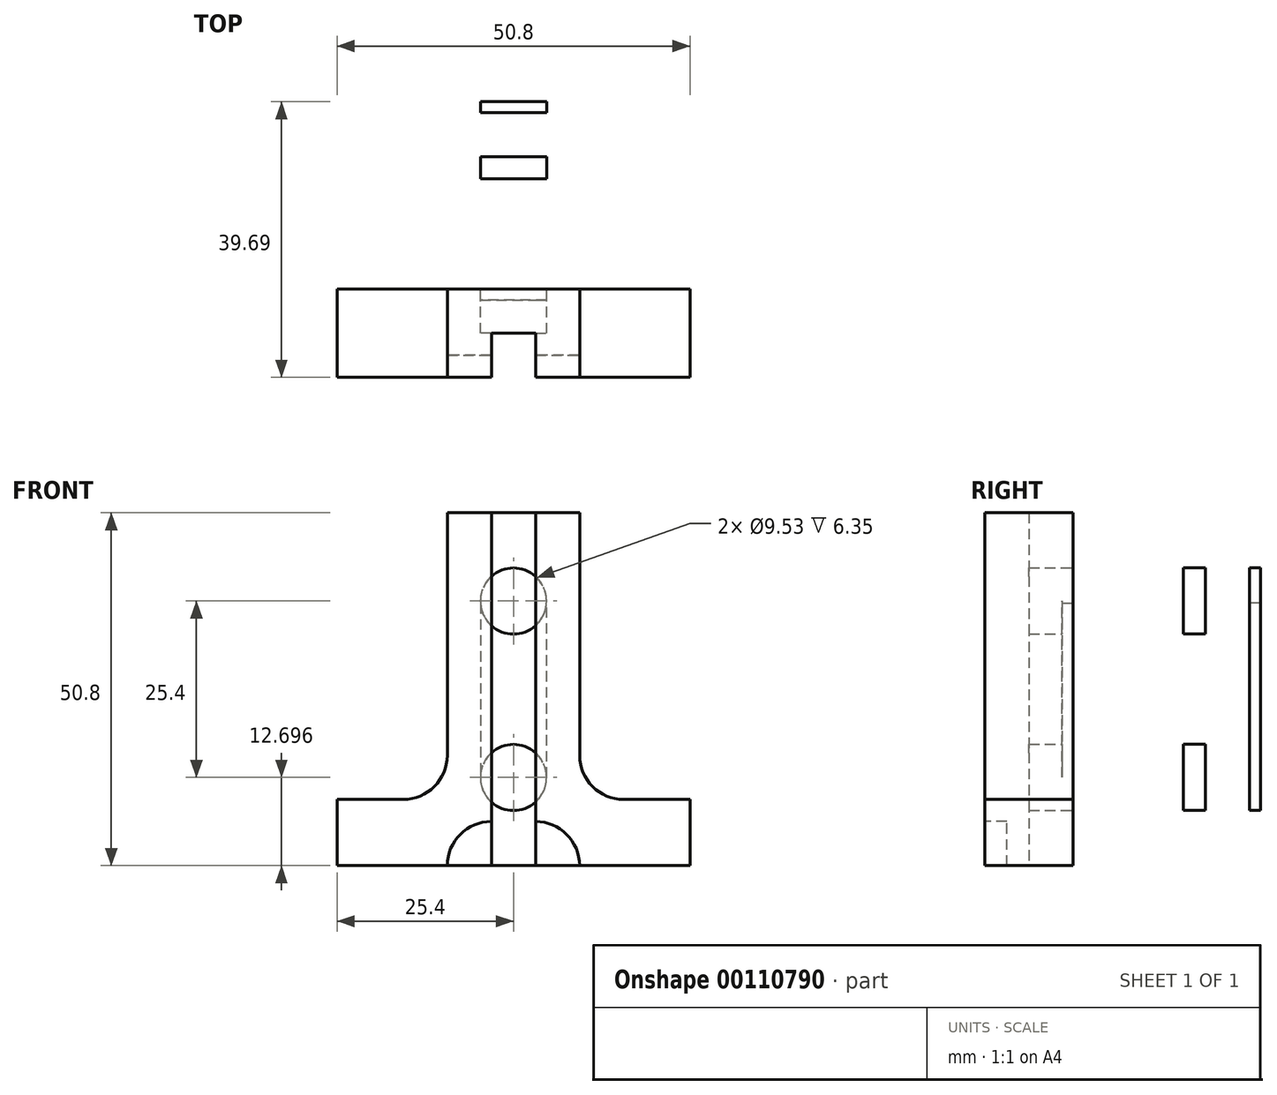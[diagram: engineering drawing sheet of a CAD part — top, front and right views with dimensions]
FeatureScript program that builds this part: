
annotation { "Feature Type Name" : "Feature", "Feature Type Description" : "" }
export const myFeature = defineFeature(function(context is Context, id is Id, definition is map)
    precondition{}
    {
        {
            var Q0;
            Q0=qCreatedBy(makeId("Front.planeOp"),FACE);
            var sketch = newSketch(context, id + "F0", { "sketchPlane" : qUnion([Q0])});
            skLineSegment(sketch, "E0.bottom", {"start": v(-9.52, 21.48) * mm, "end": v(9.53, 21.48) * mm});
            skLineSegment(sketch, "E0.top", {"start": v(-25.4, -29.32) * mm, "end": v(25.4, -29.32) * mm});
            skLineSegment(sketch, "E0.left", {"start": v(-25.4, -19.8) * mm, "end": v(-25.4, -29.32) * mm});
            skLineSegment(sketch, "E0.right", {"start": v(25.4, -19.8) * mm, "end": v(25.4, -29.32) * mm});
            skPoint(sketch, "E0.middle", {"position": v(0, -3.92) * mm});
            skLineSegment(sketch, "E1.bottom", {"start": v(-83.32, -5.3) * mm, "end": v(-91.63, -5.3) * mm});
            skLineSegment(sketch, "E1.top", {"start": v(-83.32, -3.46) * mm, "end": v(-91.63, -3.46) * mm});
            skLineSegment(sketch, "E1.left", {"start": v(-83.32, -5.3) * mm, "end": v(-83.32, -3.46) * mm});
            skLineSegment(sketch, "E1.right", {"start": v(-91.63, -5.3) * mm, "end": v(-91.63, -3.46) * mm});
            skPoint(sketch, "E1.middle", {"position": v(-87.47, -4.39) * mm});
            skLineSegment(sketch, "E2", {"start": v(-25.4, -19.8) * mm, "end": v(-15.88, -19.8) * mm});
            skLineSegment(sketch, "E3", {"start": v(-9.52, 21.48) * mm, "end": v(-9.53, -13.45) * mm});
            skPoint(sketch, "E3.endSnap0", {"position": v(0, -19.8) * mm});
            skLineSegment(sketch, "E4", {"start": v(9.53, 21.48) * mm, "end": v(9.53, -13.45) * mm});
            skPoint(sketch, "E5.orphan", {"position": v(-25.4, 21.48) * mm});
            skPoint(sketch, "E6.orphan", {"position": v(25.4, 21.48) * mm});
            skPoint(sketch, "E7.newPointA", {"position": v(-9.53, -19.8) * mm});
            skPoint(sketch, "E7.newPointB", {"position": v(25.4, -19.8) * mm});
            skArc(sketch, "E7.filletArc", {"start": v(-15.88, -19.8) * mm, "mid": v(-11.38, -17.94) * mm, "end": v(-9.53, -13.45) * mm});
            skLineSegment(sketch, "E8", {"start": v(15.87, -19.8) * mm, "end": v(25.4, -19.8) * mm});
            skPoint(sketch, "E9.visualSharp", {"position": v(9.52, -19.8) * mm});
            skArc(sketch, "E9.filletArc", {"start": v(9.52, -13.45) * mm, "mid": v(11.38, -17.94) * mm, "end": v(15.87, -19.8) * mm});
            skSolve(sketch);
        }
        {
            var Q0;
            Q0 = qSketchRegion(id + "F0", true);
            extrude(context, id + "F1", {"entities" : qUnion([Q0]), "depth" : 12.7 * mm});
        }
        {
            var Q0;
            Q0=makeQuery(id+"F1.opExtrude","CAP_FACE",FACE,{"disambiguationData":[OSD([sQuery(id+"F0.wireOp",EDGE,"E0.bottom"),sQuery(id+"F0.wireOp",EDGE,"E0.top"),sQuery(id+"F0.wireOp",EDGE,"E0.left"),sQuery(id+"F0.wireOp",EDGE,"E0.right"),sQuery(id+"F0.wireOp",EDGE,"E2"),sQuery(id+"F0.wireOp",EDGE,"E3"),sQuery(id+"F0.wireOp",EDGE,"E4"),sQuery(id+"F0.wireOp",EDGE,"E7.filletArc"),sQuery(id+"F0.wireOp",EDGE,"E8"),sQuery(id+"F0.wireOp",EDGE,"E9.filletArc")])],"isStart":false});
            var sketch = newSketch(context, id + "F2", { "sketchPlane" : qUnion([Q0])});
            skLineSegment(sketch, "E10", {"start": v(-3.18, 21.48) * mm, "end": v(-3.18, -29.32) * mm});
            skLineSegment(sketch, "E11", {"start": v(3.18, 21.48) * mm, "end": v(3.18, -29.32) * mm});
            skSolve(sketch);
        }
        {
            var Q0;
            Q0 = qSketchRegion(id + "F2", true);
            var Q1;
            {var subQ0=sQuery(id+"F2.wireOp",EDGE,"E10");Q1=makeQuery(id+"F2.imprint","IMPRINT",FACE,{"disambiguationData":[TD([[makeQuery(id+"F2.imprint","IMPRINT",EDGE,{"derivedFrom":subQ0}),1.0]])]});}
            extrude(context, id + "F3", {"entities" : qUnion([Q0, Q1]), "operationType" : NewBodyOperationType.REMOVE, "oppositeDirection" : true, "depth" : 6.35 * mm});
        }
        {
            var Q0;
            {var subQ0=sQuery(id+"F0.wireOp",EDGE,"E0.right");var subQ1=sQuery(id+"F0.wireOp",EDGE,"E0.top");var subQ2=sQuery(id+"F0.wireOp",EDGE,"E4");var subQ3=sQuery(id+"F0.wireOp",EDGE,"E0.bottom");var subQ4=sQuery(id+"F0.wireOp",EDGE,"E8");var subQ5=sQuery(id+"F0.wireOp",EDGE,"E9.filletArc");Q0=makeQuery(id+"F3.boolean.opBoolean","SPLIT",FACE,{"disambiguationData":[TD([makeQuery(id+"F1.opExtrude","SWEPT_FACE",FACE,{"disambiguationData":[OSD([subQ0])]})])],"derivedFrom":makeQuery(id+"F1.opExtrude","CAP_FACE",FACE,{"disambiguationData":[OSD([subQ3,subQ1,sQuery(id+"F0.wireOp",EDGE,"E0.left"),subQ0,sQuery(id+"F0.wireOp",EDGE,"E2"),sQuery(id+"F0.wireOp",EDGE,"E3"),subQ2,sQuery(id+"F0.wireOp",EDGE,"E7.filletArc"),subQ4,subQ5])],"isStart":false})});}
            var sketch = newSketch(context, id + "F4", { "sketchPlane" : qUnion([Q0])});
            skCircle(sketch, "E12", {"center": v(-3.18, -29.32) * mm, "radius": 6.35 * mm});
            skCircle(sketch, "E13", {"center": v(3.18, -29.32) * mm, "radius": 6.35 * mm});
            skSolve(sketch);
        }
        {
            var Q0;
            Q0 = qSketchRegion(id + "F4", true);
            extrude(context, id + "F5", {"entities" : qUnion([Q0]), "operationType" : NewBodyOperationType.REMOVE, "oppositeDirection" : true, "depth" : 3.17 * mm});
        }
        {
            var Q0;
            Q0=makeQuery(id+"F1.opExtrude","SWEPT_BODY",BODY,{"disambiguationData":[OSD([sQuery(id+"F0.wireOp",EDGE,"E1.bottom"),sQuery(id+"F0.wireOp",EDGE,"E1.top"),sQuery(id+"F0.wireOp",EDGE,"E1.left"),sQuery(id+"F0.wireOp",EDGE,"E1.right")])]});
            deleteBodies(context, id + "F6", {"entities" : qUnion([Q0])});
        }
        {
            var Q0;
            Q0=makeQuery(id+"F1.opExtrude","CAP_FACE",FACE,{"disambiguationData":[OSD([sQuery(id+"F0.wireOp",EDGE,"E0.bottom"),sQuery(id+"F0.wireOp",EDGE,"E0.top"),sQuery(id+"F0.wireOp",EDGE,"E0.left"),sQuery(id+"F0.wireOp",EDGE,"E0.right"),sQuery(id+"F0.wireOp",EDGE,"E2"),sQuery(id+"F0.wireOp",EDGE,"E3"),sQuery(id+"F0.wireOp",EDGE,"E4"),sQuery(id+"F0.wireOp",EDGE,"E7.filletArc"),sQuery(id+"F0.wireOp",EDGE,"E8"),sQuery(id+"F0.wireOp",EDGE,"E9.filletArc")])],"isStart":true});
            var sketch = newSketch(context, id + "F7", { "sketchPlane" : qUnion([Q0])});
            skCircle(sketch, "E14", {"center": v(0, 8.78) * mm, "radius": 4.76 * mm});
            skCircle(sketch, "E15", {"center": v(0, -16.62) * mm, "radius": 4.76 * mm});
            skLineSegment(sketch, "E16", {"start": v(4.75, 8.46) * mm, "end": v(4.76, -16.62) * mm});
            skLineSegment(sketch, "E17", {"start": v(-4.76, -16.62) * mm, "end": v(-4.76, 8.78) * mm});
            skSolve(sketch);
        }
        {
            var Q0;
            {var subQ0=sQuery(id+"F7.wireOp",EDGE,"E16");Q0=makeQuery(id+"F7.imprint","IMPRINT",FACE,{"disambiguationData":[TD([[makeQuery(id+"F7.imprint","IMPRINT",EDGE,{"derivedFrom":subQ0}),-1.0]])]});}
            var Q1;
            {var subQ0=sQuery(id+"F7.wireOp",EDGE,"E14");var subQ1=makeQuery(id+"F7.imprint","INTERSECT",VERTEX,{"derivedFrom":[subQ0,sQuery(id+"F7.wireOp",EDGE,"E16")]});Q1=makeQuery(id+"F7.imprint","IMPRINT",FACE,{"disambiguationData":[TD([[makeQuery(id+"F7.imprint","IMPRINT",EDGE,{"disambiguationData":[TD([[subQ1,1.0]])],"derivedFrom":subQ0}),1.0]])]});}
            var Q2;
            {var subQ0=sQuery(id+"F7.wireOp",EDGE,"E15");var subQ1=makeQuery(id+"F7.imprint","INTERSECT",VERTEX,{"derivedFrom":[subQ0,sQuery(id+"F7.wireOp",EDGE,"E16")]});Q2=makeQuery(id+"F7.imprint","IMPRINT",FACE,{"disambiguationData":[TD([[makeQuery(id+"F7.imprint","IMPRINT",EDGE,{"disambiguationData":[TD([[subQ1,-1.0]])],"derivedFrom":subQ0}),1.0]])]});}
            extrude(context, id + "F8", {"entities" : qUnion([Q0, Q1, Q2]), "operationType" : NewBodyOperationType.REMOVE, "oppositeDirection" : true, "depth" : 1.6 * mm});
        }
        {
            var Q0;
            Q0 = qSketchRegion(id + "F7", true);
            var Q1;
            Q1=makeQuery(id+"F8.boolean.opBoolean","COPY",FACE,{"derivedFrom":makeQuery(id+"F8.opExtrude","CAP_FACE",FACE,{"disambiguationData":[OSD([sQuery(id+"F7.wireOp",EDGE,"E14"),sQuery(id+"F7.wireOp",EDGE,"E15"),sQuery(id+"F7.wireOp",EDGE,"E16"),sQuery(id+"F7.wireOp",EDGE,"E17")])],"isStart":false})});
            extrude(context, id + "F9", {"entities" : qUnion([Q0, Q1]), "depth" : 26.99 * mm, "hasSecondDirection" : true, "secondDirectionOppositeDirection" : false, "secondDirectionDepth" : 25.4 * mm});
        }
        {
            var Q0;
            {var subQ0=sQuery(id+"F7.wireOp",EDGE,"E17");var subQ1=sQuery(id+"F7.wireOp",EDGE,"E16");var subQ2=sQuery(id+"F7.wireOp",EDGE,"E15");var subQ3=sQuery(id+"F7.wireOp",EDGE,"E14");Q0=makeQuery(id+"F9.opExtrude","SWEPT_BODY",BODY,{"disambiguationData":[OSD([subQ3,subQ2,subQ1,subQ0]),TDD([makeQuery(id+"F8.boolean.opBoolean","COPY",FACE,{"derivedFrom":makeQuery(id+"F8.opExtrude","CAP_FACE",FACE,{"disambiguationData":[OSD([subQ3,subQ2,subQ1,subQ0])],"isStart":false})})])]});}
            deleteBodies(context, id + "F10", {"entities" : qUnion([Q0])});
        }
        {
            var Q0;
            Q0=makeQuery(id+"F1.opExtrude","CAP_FACE",FACE,{"disambiguationData":[OSD([sQuery(id+"F0.wireOp",EDGE,"E0.bottom"),sQuery(id+"F0.wireOp",EDGE,"E0.top"),sQuery(id+"F0.wireOp",EDGE,"E0.left"),sQuery(id+"F0.wireOp",EDGE,"E0.right"),sQuery(id+"F0.wireOp",EDGE,"E2"),sQuery(id+"F0.wireOp",EDGE,"E3"),sQuery(id+"F0.wireOp",EDGE,"E4"),sQuery(id+"F0.wireOp",EDGE,"E7.filletArc"),sQuery(id+"F0.wireOp",EDGE,"E8"),sQuery(id+"F0.wireOp",EDGE,"E9.filletArc")])],"isStart":true});
            var sketch = newSketch(context, id + "F11", { "sketchPlane" : qUnion([Q0])});
            skCircle(sketch, "E18", {"center": v(0, 8.78) * mm, "radius": 4.76 * mm});
            skCircle(sketch, "E19", {"center": v(0, -16.62) * mm, "radius": 4.76 * mm});
            skSolve(sketch);
        }
        {
            var Q0;
            Q0 = qSketchRegion(id + "F11", true);
            extrude(context, id + "F12", {"entities" : qUnion([Q0]), "operationType" : NewBodyOperationType.REMOVE, "oppositeDirection" : true, "depth" : 6.35 * mm});
        }
        {
            var Q0;
            Q0 = qSketchRegion(id + "F11", true);
            extrude(context, id + "F13", {"entities" : qUnion([Q0]), "depth" : 19.05 * mm, "hasSecondDirection" : true, "secondDirectionOppositeDirection" : false, "secondDirectionDepth" : 15.88 * mm});
        }
    });
